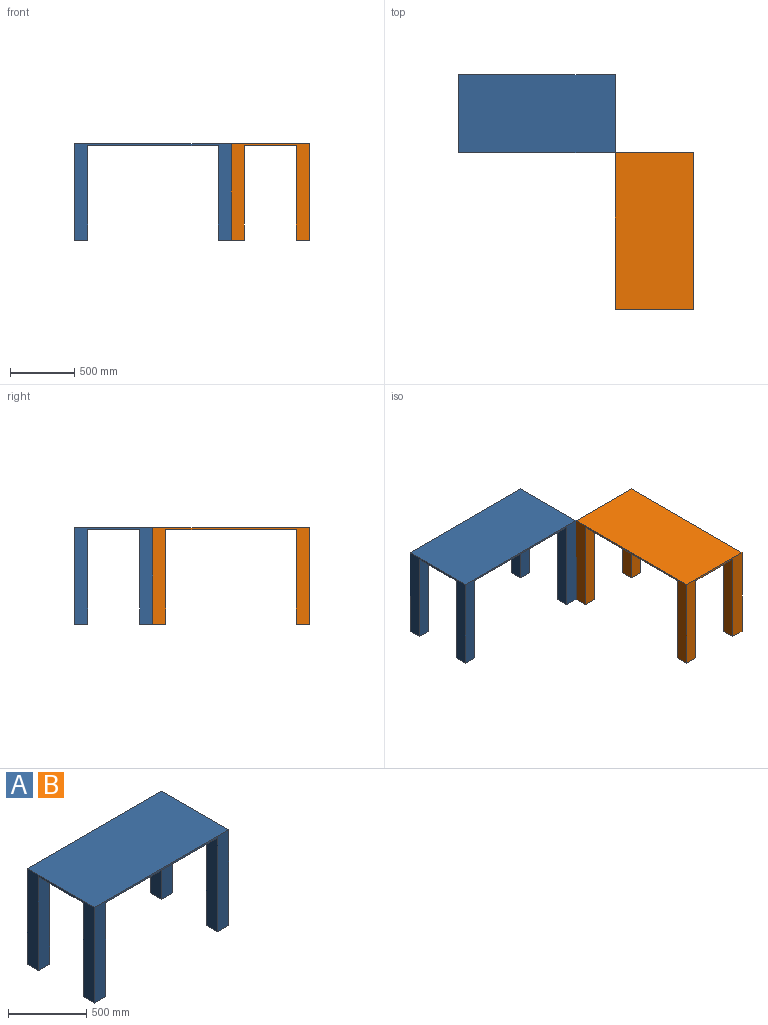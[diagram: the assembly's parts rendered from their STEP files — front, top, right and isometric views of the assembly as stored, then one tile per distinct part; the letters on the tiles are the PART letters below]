
ASSEMBLY  parts=2 mates=1
PART A: 18 faces, bbox 1219.2x609.6x749.3 mm
  f0: plane 749.3x609.6mm, normal (1,0,0), area 157419mm2, adj f1,f3,f4,f5,f9,f11,f12,f14
  f1: plane 1219.2x749.3mm, normal (0,1,0), area 165161mm2, adj f0,f2,f4,f5,f13,f14,f16,f17
  f2: plane 749.3x609.6mm, normal (-1,0,0), area 157419mm2, adj f1,f3,f4,f5,f6,f8,f15,f17
  f3: plane 1219.2x749.3mm, normal (0,-1,0), area 165161mm2, adj f0,f2,f4,f5,f7,f8,f10,f11
  f4: plane 1219.2x609.6mm, normal (0,0,1), area 743224.3mm2, adj f0,f1,f2,f3
  f5: plane 1219.2x609.6mm, normal (0,0,-1), area 701934.1mm2, adj f0,f1,f2,f3,f6,f7,f9,f10
  f6: plane 736.6x101.6mm, normal (0,1,0), area 74838.6mm2, adj f2,f5,f7,f8
  f7: plane 736.6x101.6mm, normal (1,0,0), area 74838.6mm2, adj f3,f5,f6,f8
  f8: plane 101.6x101.6mm, normal (0,0,-1), area 10322.6mm2, adj f2,f3,f6,f7
  f9: plane 736.6x101.6mm, normal (0,1,0), area 74838.6mm2, adj f0,f5,f10,f11
  f10: plane 736.6x101.6mm, normal (-1,0,0), area 74838.6mm2, adj f3,f5,f9,f11
  f11: plane 101.6x101.6mm, normal (0,0,-1), area 10322.6mm2, adj f0,f3,f9,f10
  f12: plane 736.6x101.6mm, normal (0,-1,0), area 74838.6mm2, adj f0,f5,f13,f14
  f13: plane 736.6x101.6mm, normal (-1,0,0), area 74838.6mm2, adj f1,f5,f12,f14
  f14: plane 101.6x101.6mm, normal (0,0,-1), area 10322.6mm2, adj f0,f1,f12,f13
  f15: plane 736.6x101.6mm, normal (0,-1,0), area 74838.6mm2, adj f2,f5,f16,f17
  f16: plane 736.6x101.6mm, normal (1,0,0), area 74838.6mm2, adj f1,f5,f15,f17
  f17: plane 101.6x101.6mm, normal (0,0,-1), area 10322.6mm2, adj f1,f2,f15,f16
PART B: same geometry as A
PLACE A t=(864.7,616.51,334.59)mm
PLACE B rot(axis=(0,0,-1),90deg) t=(1779.1,-297.89,334.59)mm
MATE fastened A.f0 <-> B.f3  axis (1,0,0) through (1474.3,311.71,347.29)mm
